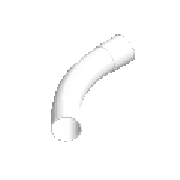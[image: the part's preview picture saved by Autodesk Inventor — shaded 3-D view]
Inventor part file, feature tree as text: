
AUTODESK INVENTOR PART (.ipt)
format: ipt  version: 2023 (Build 270158000, 158)  size: 243,712 bytes
history: native  units: mm (DEFAULTED — no unit token found)
features: other x6, sketch x2, revolve x2, sweep x1
ambient origin geometry x8: Origin, YZ Plane, XZ Plane, XY Plane, X Axis, Y Axis, Z Axis, Center Point
bodies: Solid1 (feature_tree)
feature tree (11):
  sketch  "Sketch1"  dims[d0=91.0mm d1=110.0mm]
  revolve  "Revolve1"  [1 undecoded]
  revolve  "Revolve2"  [1 undecoded]
  sweep  "Sweep3"
  other  "Work Point1"
  other  "Work Point2"
  other  "Work Axis1"
  other  "Work Point3"
  other  "Work Axis2"
  other  "Work Point4"
  sketch  "Sketch2"  dims[d2=3.2mm d3=3.2mm d4=4.8mm d5=45.0deg d6=91.0mm d7=3.2mm d8=4.8mm d9=110.0mm d10=3.2mm d11=203.0mm d12=203.0mm d13=2.56mm d14=3.2mm d99=90.0deg d100=90.0deg d15=0.0mm d16=3.2mm d104=0.0mm]
note: 2 required parameter values undecoded (feature->parameter linkage not recoverable at this tier; creation-order binding heuristic only, values carry confidence <= 0.55)
